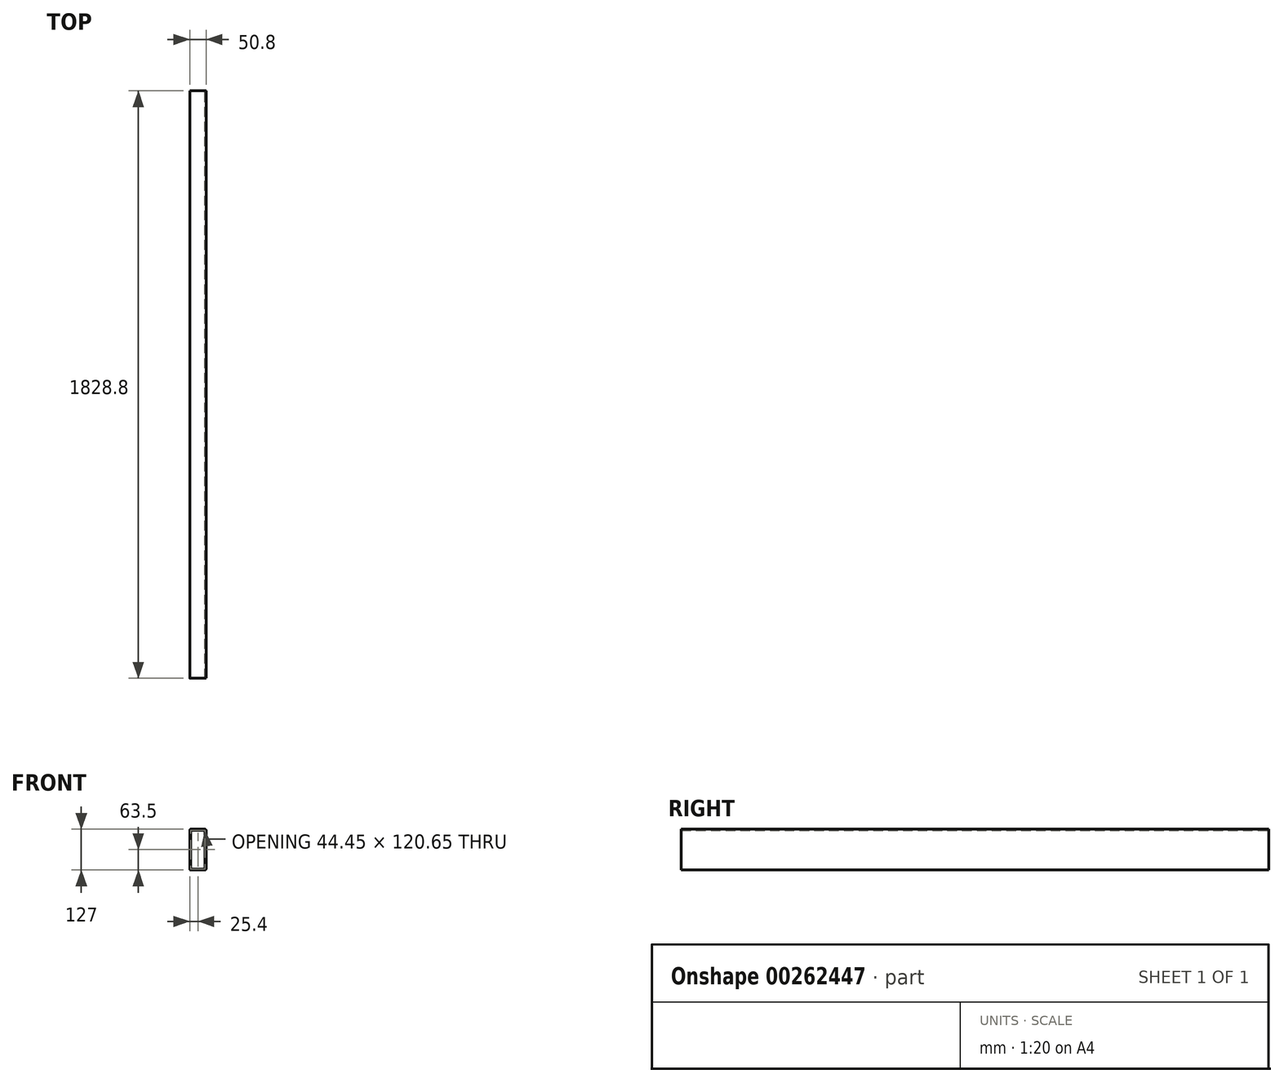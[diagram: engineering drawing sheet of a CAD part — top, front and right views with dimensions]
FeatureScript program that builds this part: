
annotation { "Feature Type Name" : "Feature", "Feature Type Description" : "" }
export const myFeature = defineFeature(function(context is Context, id is Id, definition is map)
    precondition{}
    {
        {
            var Q0;
            Q0=qCreatedBy(makeId("Front.planeOp"),FACE);
            var sketch = newSketch(context, id + "F0", { "sketchPlane" : qUnion([Q0])});
            skLineSegment(sketch, "E0.bottom", {"start": v(22.22, 63.5) * mm, "end": v(-22.23, 63.5) * mm});
            skLineSegment(sketch, "E0.top", {"start": v(22.23, -63.5) * mm, "end": v(-22.22, -63.5) * mm});
            skLineSegment(sketch, "E0.left", {"start": v(25.4, 60.33) * mm, "end": v(25.4, -60.33) * mm});
            skLineSegment(sketch, "E0.right", {"start": v(-25.4, 60.32) * mm, "end": v(-25.4, -60.33) * mm});
            skPoint(sketch, "E0.middle", {"position": v(0, 0) * mm});
            skLineSegment(sketch, "E1.bottom", {"start": v(19.05, 60.33) * mm, "end": v(-19.05, 60.33) * mm});
            skLineSegment(sketch, "E1.top", {"start": v(19.05, -60.33) * mm, "end": v(-19.05, -60.33) * mm});
            skLineSegment(sketch, "E1.left", {"start": v(22.22, 57.15) * mm, "end": v(22.23, -57.15) * mm});
            skLineSegment(sketch, "E1.right", {"start": v(-22.23, 57.15) * mm, "end": v(-22.22, -57.15) * mm});
            skPoint(sketch, "E2.visualSharp", {"position": v(-25.4, 63.5) * mm});
            skArc(sketch, "E2.filletArc", {"start": v(-22.23, 63.5) * mm, "mid": v(-24.47, 62.57) * mm, "end": v(-25.4, 60.32) * mm});
            skPoint(sketch, "E3.visualSharp", {"position": v(-22.23, 60.33) * mm});
            skArc(sketch, "E3.filletArc", {"start": v(-19.05, 60.32) * mm, "mid": v(-21.3, 59.4) * mm, "end": v(-22.23, 57.15) * mm});
            skPoint(sketch, "E4.visualSharp", {"position": v(25.4, 63.5) * mm});
            skArc(sketch, "E4.filletArc", {"start": v(25.4, 60.33) * mm, "mid": v(24.47, 62.57) * mm, "end": v(22.22, 63.5) * mm});
            skArc(sketch, "E5.filletArc", {"start": v(22.22, 57.15) * mm, "mid": v(21.3, 59.4) * mm, "end": v(19.05, 60.33) * mm});
            skPoint(sketch, "E6.visualSharp", {"position": v(-25.4, -63.5) * mm});
            skArc(sketch, "E6.filletArc", {"start": v(-25.4, -60.33) * mm, "mid": v(-24.47, -62.57) * mm, "end": v(-22.22, -63.5) * mm});
            skArc(sketch, "E7.filletArc", {"start": v(-22.22, -57.15) * mm, "mid": v(-21.3, -59.4) * mm, "end": v(-19.05, -60.32) * mm});
            skPoint(sketch, "E8.visualSharp", {"position": v(22.23, -60.33) * mm});
            skArc(sketch, "E8.filletArc", {"start": v(19.05, -60.32) * mm, "mid": v(21.3, -59.4) * mm, "end": v(22.22, -57.15) * mm});
            skPoint(sketch, "E9.visualSharp", {"position": v(25.4, -63.5) * mm});
            skArc(sketch, "E9.filletArc", {"start": v(22.23, -63.5) * mm, "mid": v(24.47, -62.57) * mm, "end": v(25.4, -60.33) * mm});
            skSolve(sketch);
        }
        {
            var Q0;
            Q0 = qSketchRegion(id + "F0", true);
            extrude(context, id + "F1", {"entities" : qUnion([Q0]), "depth" : 1828.8 * mm});
        }
    });
